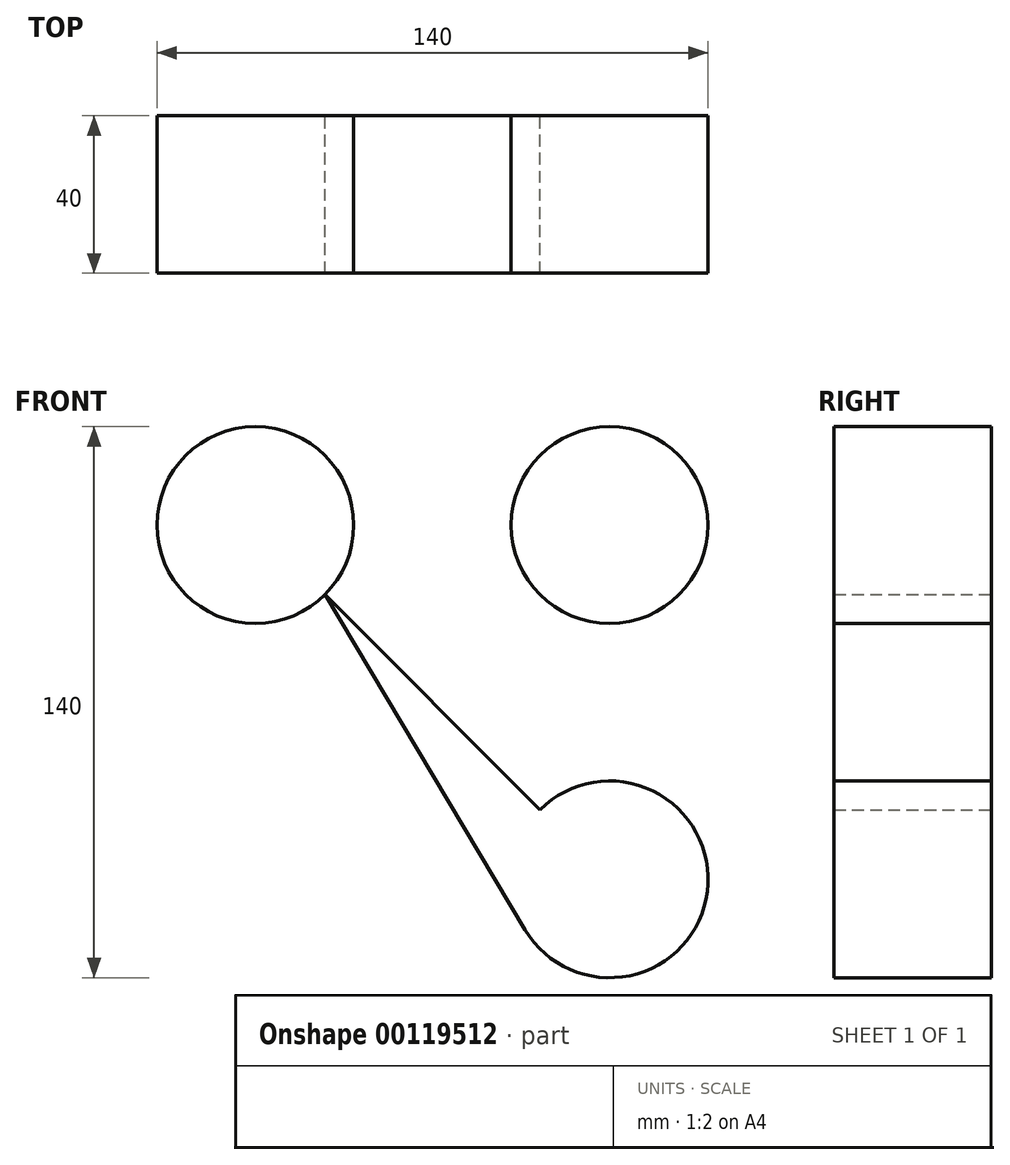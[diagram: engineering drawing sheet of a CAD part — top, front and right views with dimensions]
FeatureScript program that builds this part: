
annotation { "Feature Type Name" : "Feature", "Feature Type Description" : "" }
export const myFeature = defineFeature(function(context is Context, id is Id, definition is map)
    precondition{}
    {
        {
            var Q0;
            Q0=qCreatedBy(makeId("Front.planeOp"),FACE);
            var sketch = newSketch(context, id + "F0", { "sketchPlane" : qUnion([Q0])});
            skCircle(sketch, "E0", {"center": v(0, 0) * mm, "radius": 25 * mm});
            skCircle(sketch, "E1", {"center": v(0, 90) * mm, "radius": 25 * mm});
            skCircle(sketch, "E2", {"center": v(-90, 90) * mm, "radius": 25 * mm});
            skLineSegment(sketch, "E3", {"start": v(0, 0) * mm, "end": v(-90, 90) * mm});
            skLineSegment(sketch, "E4", {"start": v(0, 90) * mm, "end": v(-90, 90) * mm, "construction": true});
            skLineSegment(sketch, "E5", {"start": v(0, 90) * mm, "end": v(0, 0) * mm});
            skLineSegment(sketch, "E6", {"start": v(-72.32, 72.32) * mm, "end": v(-21.46, -12.82) * mm});
            skSolve(sketch);
        }
        {
            var Q0;
            Q0 = qSketchRegion(id + "F0", true);
            extrude(context, id + "F1", {"entities" : qUnion([Q0]), "endBound" : BoundingType.SYMMETRIC, "depth" : 40 * mm});
        }
    });
